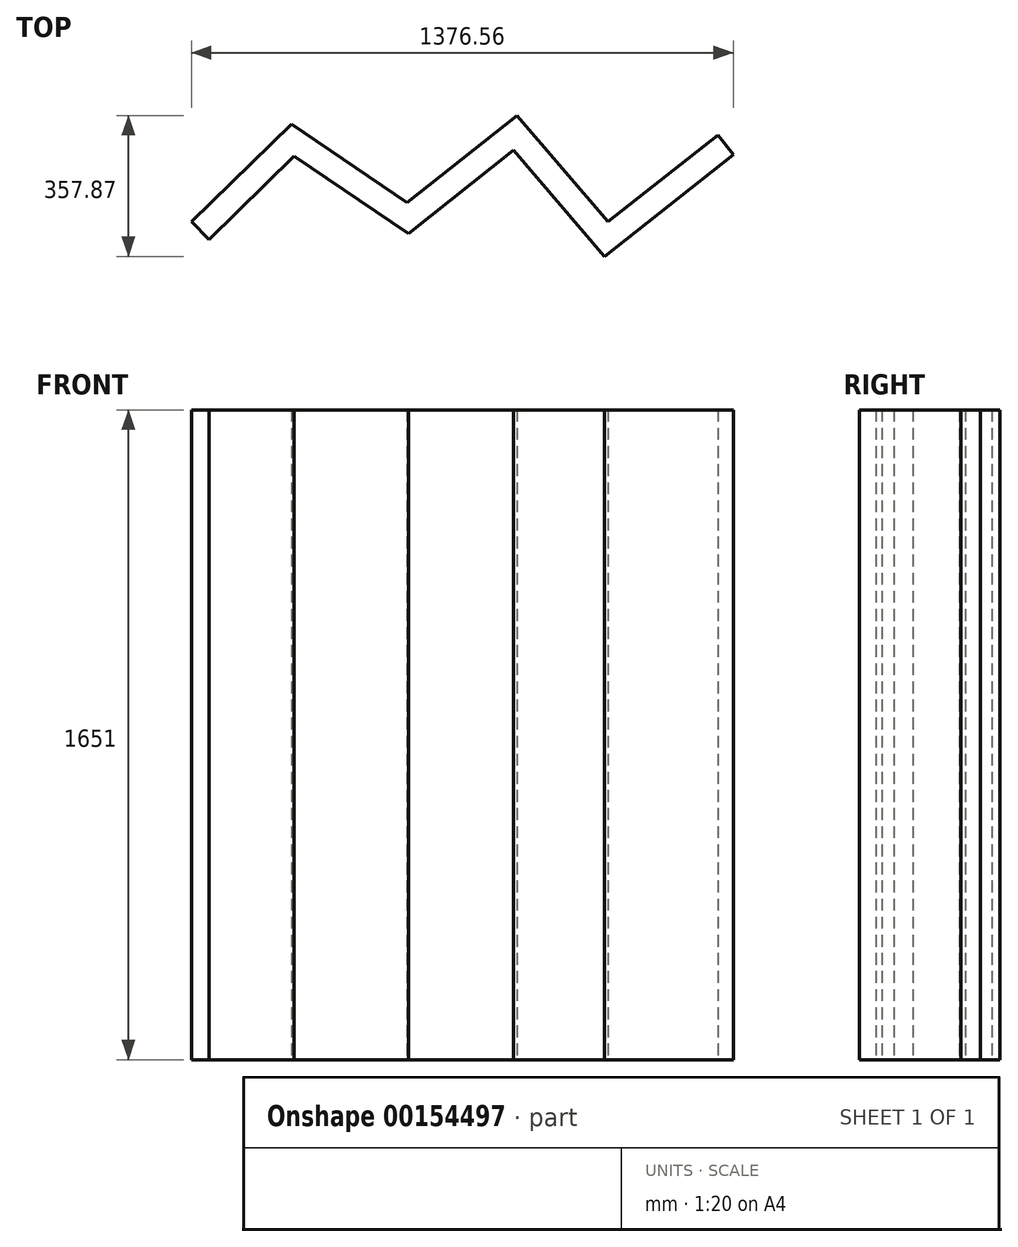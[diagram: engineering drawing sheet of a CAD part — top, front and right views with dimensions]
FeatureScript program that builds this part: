
annotation { "Feature Type Name" : "Feature", "Feature Type Description" : "" }
export const myFeature = defineFeature(function(context is Context, id is Id, definition is map)
    precondition{}
    {
        {
            var Q0;
            Q0=qCreatedBy(makeId("Top.planeOp"),FACE);
            var sketch = newSketch(context, id + "F0", { "sketchPlane" : qUnion([Q0])});
            skLineSegment(sketch, "E0", {"start": v(0, 0) * mm, "end": v(254, 248.87) * mm});
            skLineSegment(sketch, "E1", {"start": v(254, 248.87) * mm, "end": v(548.38, 49.4) * mm});
            skLineSegment(sketch, "E2", {"start": v(548.38, 49.4) * mm, "end": v(827.16, 270.17) * mm});
            skLineSegment(sketch, "E3", {"start": v(827.16, 270.17) * mm, "end": v(1058.37, 0) * mm});
            skLineSegment(sketch, "E4", {"start": v(1058.37, 0) * mm, "end": v(1337.14, 220.76) * mm});
            skLineSegment(sketch, "E5", {"start": v(0, 0) * mm, "end": v(44.44, -45.36) * mm});
            skLineSegment(sketch, "E6", {"start": v(44.44, -45.36) * mm, "end": v(261.35, 167.18) * mm});
            skLineSegment(sketch, "E7", {"start": v(261.35, 167.18) * mm, "end": v(551.3, -29.28) * mm});
            skLineSegment(sketch, "E8", {"start": v(551.3, -29.28) * mm, "end": v(818.7, 182.47) * mm});
            skLineSegment(sketch, "E9", {"start": v(818.7, 182.47) * mm, "end": v(1049.9, -87.7) * mm});
            skLineSegment(sketch, "E10", {"start": v(1049.9, -87.7) * mm, "end": v(1376.56, 170.98) * mm});
            skLineSegment(sketch, "E11", {"start": v(1376.56, 170.98) * mm, "end": v(1337.14, 220.76) * mm});
            skLineSegment(sketch, "E12", {"start": v(324.9, 124.13) * mm, "end": v(360.51, 176.7) * mm, "construction": true});
            skLineSegment(sketch, "E13", {"start": v(649.63, 129.59) * mm, "end": v(689.05, 79.8) * mm, "construction": true});
            skLineSegment(sketch, "E14", {"start": v(883.64, 106.58) * mm, "end": v(933.42, 146) * mm, "construction": true});
            skSolve(sketch);
        }
        {
            var Q0;
            Q0=makeQuery(id+"F0.imprint","IMPRINT",FACE,{"disambiguationData":[TD([[makeQuery(id+"F0.imprint","IMPRINT",EDGE,{"derivedFrom":sQuery(id+"F0.wireOp",EDGE,"E0")}),-1.0]])]});
            extrude(context, id + "F1", {"entities" : qUnion([Q0]), "depth" : 1651 * mm});
        }
    });
